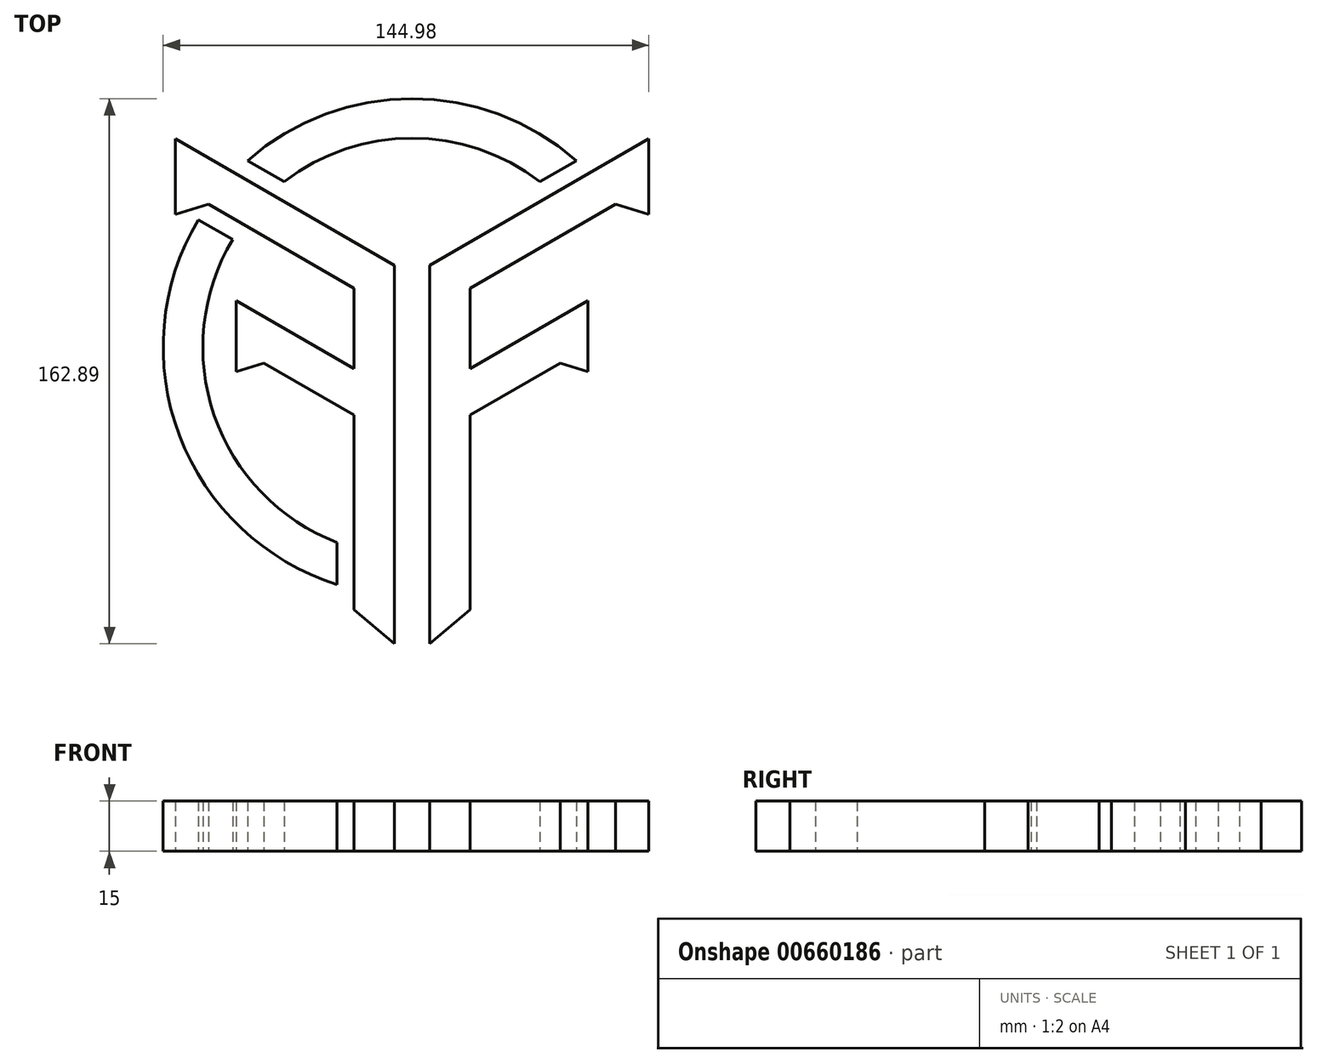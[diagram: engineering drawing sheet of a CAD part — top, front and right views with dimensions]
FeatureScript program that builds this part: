
annotation { "Feature Type Name" : "Feature", "Feature Type Description" : "" }
export const myFeature = defineFeature(function(context is Context, id is Id, definition is map)
    precondition{}
    {
        {
            var Q0;
            Q0=qCreatedBy(makeId("Top.planeOp"),FACE);
            var sketch = newSketch(context, id + "F0", { "sketchPlane" : qUnion([Q0])});
            skLineSegment(sketch, "E0", {"start": v(-5.3, -88.6) * mm, "end": v(-5.3, 24.5) * mm});
            skLineSegment(sketch, "E1", {"start": v(-5.3, 24.5) * mm, "end": v(-70.68, 62.28) * mm});
            skLineSegment(sketch, "E2", {"start": v(-70.68, 62.28) * mm, "end": v(-70.68, 39.67) * mm});
            skLineSegment(sketch, "E3", {"start": v(-70.68, 39.67) * mm, "end": v(-60.8, 42.71) * mm});
            skLineSegment(sketch, "E4", {"start": v(-60.8, 42.71) * mm, "end": v(-17.3, 17.58) * mm});
            skLineSegment(sketch, "E5", {"start": v(-17.3, -78.4) * mm, "end": v(-5.3, -88.6) * mm});
            skLineSegment(sketch, "E6", {"start": v(-17.3, -6.42) * mm, "end": v(-52.55, 13.95) * mm});
            skLineSegment(sketch, "E7", {"start": v(-52.55, 13.95) * mm, "end": v(-52.55, -7.28) * mm});
            skLineSegment(sketch, "E8", {"start": v(-52.55, -7.28) * mm, "end": v(-44.22, -4.72) * mm});
            skLineSegment(sketch, "E9", {"start": v(-44.22, -4.72) * mm, "end": v(-17.3, -20.27) * mm});
            skLineSegment(sketch, "E10", {"start": v(-49.11, 55.75) * mm, "end": v(-38.18, 49.44) * mm});
            skLineSegment(sketch, "E11", {"start": v(-63.8, 38.07) * mm, "end": v(-53.56, 32.15) * mm});
            skLineSegment(sketch, "E12", {"start": v(-22.36, -58.33) * mm, "end": v(-22.36, -70.86) * mm});
            skArc(sketch, "E13", {"start": v(-53.56, 32.15) * mm, "mid": v(-59.06, -20.36) * mm, "end": v(-22.36, -58.33) * mm});
            skArc(sketch, "E14", {"start": v(-63.8, 38.07) * mm, "mid": v(-69.44, -26.42) * mm, "end": v(-22.36, -70.86) * mm});
            skArc(sketch, "E15", {"start": v(-38.18, 49.44) * mm, "mid": v(-20.17, 59.12) * mm, "end": v(0, 62.47) * mm});
            skArc(sketch, "E16", {"start": v(-49.11, 55.75) * mm, "mid": v(-26.25, 69.5) * mm, "end": v(0, 74.3) * mm});
            skLineSegment(sketch, "E17", {"start": v(-17.3, 17.58) * mm, "end": v(-17.3, -6.42) * mm});
            skLineSegment(sketch, "E18", {"start": v(-17.3, -20.27) * mm, "end": v(-17.3, -78.4) * mm});
            skArc(sketch, "E19.MirrorCS", {"start": v(49.11, 55.75) * mm, "mid": v(26.25, 69.5) * mm, "end": v(0, 74.3) * mm});
            skArc(sketch, "E20.MirrorCS", {"start": v(63.8, 38.07) * mm, "mid": v(69.44, -26.42) * mm, "end": v(22.36, -70.86) * mm});
            skLineSegment(sketch, "E21.MirrorCS", {"start": v(17.3, 17.58) * mm, "end": v(17.3, -6.42) * mm});
            skLineSegment(sketch, "E22.MirrorCS", {"start": v(17.3, -20.27) * mm, "end": v(17.3, -78.4) * mm});
            skLineSegment(sketch, "E23.MirrorCS", {"start": v(44.22, -4.72) * mm, "end": v(17.3, -20.27) * mm});
            skLineSegment(sketch, "E24.MirrorCS", {"start": v(17.3, -78.4) * mm, "end": v(5.3, -88.6) * mm});
            skLineSegment(sketch, "E25.MirrorCS", {"start": v(60.8, 42.71) * mm, "end": v(17.3, 17.58) * mm});
            skLineSegment(sketch, "E26.MirrorCS", {"start": v(52.55, -7.28) * mm, "end": v(44.22, -4.72) * mm});
            skArc(sketch, "E27.MirrorCS", {"start": v(53.56, 32.15) * mm, "mid": v(59.06, -20.36) * mm, "end": v(22.36, -58.33) * mm});
            skLineSegment(sketch, "E28.MirrorCS", {"start": v(17.3, -6.42) * mm, "end": v(52.55, 13.95) * mm});
            skArc(sketch, "E29.MirrorCS", {"start": v(38.18, 49.44) * mm, "mid": v(20.17, 59.12) * mm, "end": v(0, 62.47) * mm});
            skLineSegment(sketch, "E30.MirrorCS", {"start": v(70.68, 39.67) * mm, "end": v(60.8, 42.71) * mm});
            skLineSegment(sketch, "E31.MirrorCS", {"start": v(52.55, 13.95) * mm, "end": v(52.55, -7.28) * mm});
            skLineSegment(sketch, "E32.MirrorCS", {"start": v(49.11, 55.75) * mm, "end": v(38.18, 49.44) * mm});
            skLineSegment(sketch, "E33.MirrorCS", {"start": v(5.3, -88.6) * mm, "end": v(5.3, 24.5) * mm});
            skLineSegment(sketch, "E34.MirrorCS", {"start": v(5.3, 24.5) * mm, "end": v(70.68, 62.28) * mm});
            skLineSegment(sketch, "E35.MirrorCS", {"start": v(63.8, 38.07) * mm, "end": v(53.56, 32.15) * mm});
            skLineSegment(sketch, "E36.MirrorCS", {"start": v(22.36, -58.33) * mm, "end": v(22.36, -70.86) * mm});
            skLineSegment(sketch, "E37.MirrorCS", {"start": v(70.68, 62.28) * mm, "end": v(70.68, 39.67) * mm});
            skSolve(sketch);
        }
        {
            var Q0;
            Q0=makeQuery(id+"F0.imprint","IMPRINT",FACE,{"disambiguationData":[TD([[makeQuery(id+"F0.imprint","IMPRINT",EDGE,{"derivedFrom":sQuery(id+"F0.wireOp",EDGE,"E10")}),1.0]])]});
            var Q1;
            Q1=makeQuery(id+"F0.imprint","IMPRINT",FACE,{"disambiguationData":[TD([[makeQuery(id+"F0.imprint","IMPRINT",EDGE,{"derivedFrom":sQuery(id+"F0.wireOp",EDGE,"E11")}),-1.0]])]});
            var Q2;
            Q2=makeQuery(id+"F0.imprint","IMPRINT",FACE,{"disambiguationData":[TD([[makeQuery(id+"F0.imprint","IMPRINT",EDGE,{"derivedFrom":sQuery(id+"F0.wireOp",EDGE,"E20.MirrorCS")}),-1.0]])]});
            var Q3;
            Q3=makeQuery(id+"F0.imprint","IMPRINT",FACE,{"disambiguationData":[TD([[makeQuery(id+"F0.imprint","IMPRINT",EDGE,{"derivedFrom":sQuery(id+"F0.wireOp",EDGE,"E0")}),1.0]])]});
            var Q4;
            Q4=makeQuery(id+"F0.imprint","IMPRINT",FACE,{"disambiguationData":[TD([[makeQuery(id+"F0.imprint","IMPRINT",EDGE,{"derivedFrom":sQuery(id+"F0.wireOp",EDGE,"E21.MirrorCS")}),-1.0]])]});
            extrude(context, id + "F1", {"entities" : qUnion([Q0, Q1, Q2, Q3, Q4]), "depth" : 15 * mm, "offsetDistance" : 25 * mm});
        }
    });
